# Revit family: Neri_Light 21_SU213L-Pooo
name_source: partatom
category: Apparecchi per illuminazione
revit_build: Autodesk Revit LT 2018 (Build: 20170223_1515(x64)
units: mm (PartAtom-declared; Revit-internal decimal feet)

## family parameters
Basato su piano di lavoro = No
Condiviso = No
Numero OmniClass = 23.35.47.11
Punto di calcolo locali = No
Quota connettore circolare = Usa diametro
Sempre verticale = Sì
Sorgente d'illuminazione = Sì
Taglio con vuoti quando caricato = No
Tipo di parte = Normale

## types (2) — shared parameters
Angolo inclinazione = 90.00°
CRI = >70
Class IES = CutOff
Connection = Suspended installation with threaded tube G 3/4"
tube (G 3/4"
Control = COD 02= 1-10V + NCL, COD 06= DALI + NCL, COD 14= NVL6H + NCL
Data Sheet = https://www.nerinorthamerica.com
Design Country = Italy
Diametre = 1' - 9 3/4"
EPA = 0.484 ft²
Estimated Life = 80.000 h (L85 - Ta 25°C)
Fasteners = Stainless Steel
Filtro dei colori = 16777215
Frequency = 50-60 Hz
Height = 11' - 1/8"
Height of Installation = 11.5' to 16.5'
IK = 10
IP = 66
Immagine tipo = <Nessuno>
Installation Instructions = https://www.nerinorthamerica.com 21_LED-P_2016C.pdf
LOR = 100 %
Lampada = LED
Luminous Efficacy = 94 Lm/W
Manufacturer Country = Italy
Manufacturer Name = Neri SpA
MasterFormat 2016 Code = 26 56 00
MasterFormat 2016 Description = Exterior Lighting
Material Main = Die-Cast and Sheet Aluminum
Material Secondary = Hot galvanized steel
Modello = SU213L-P
NBS_UniClass2015 Code = Ss_70_80_25_70
NBS_UniClass2015 Description = Roadway Lighting Systems
OmniClass Code = 23-35 47 11
OmniClass Description = Lighting Fixtures
Operative Temperature = -22F°/ +104F°
Overvoltage protection = 4kV/4kV (differential / common mode)
Painting = Standard color Dark Grey, type Neri - On demand features - Painting:colour of RAL range
Painting Steps = Information about paint steps used in this product in specific technical sheet
Product Certification = UL Standard 1598 (C, US)
Product Name = Light 21 - LED P
Produttore = Neri SpA
URL = https://www.nerinorthamerica.com
UniFormat II Code = D5020
UniFormat II Description = Lighting and Branch Wiring
Variazione temperatura colore lampada con luminosità attenuata = <Nessuno>
Voltage = 120-277 V
W = 48
Weight = 17.63 lb

## per-type parameters (varying)
| type | File diagramma fotometrico | Lighting Distribution/Class | Luminaire Classification System | Optics |
| SU213L_NLG02 | SU213L_NLG02.IES | Asymmetrical - Type III - Short | BUG: B1 U0 G1 | NLG02 |
| SU213L_NLG06 | SU213L_NLG06.IES | Rotosymmetrical - Type V - Short | BUG: B2 U0 G0 | NLG06 |
